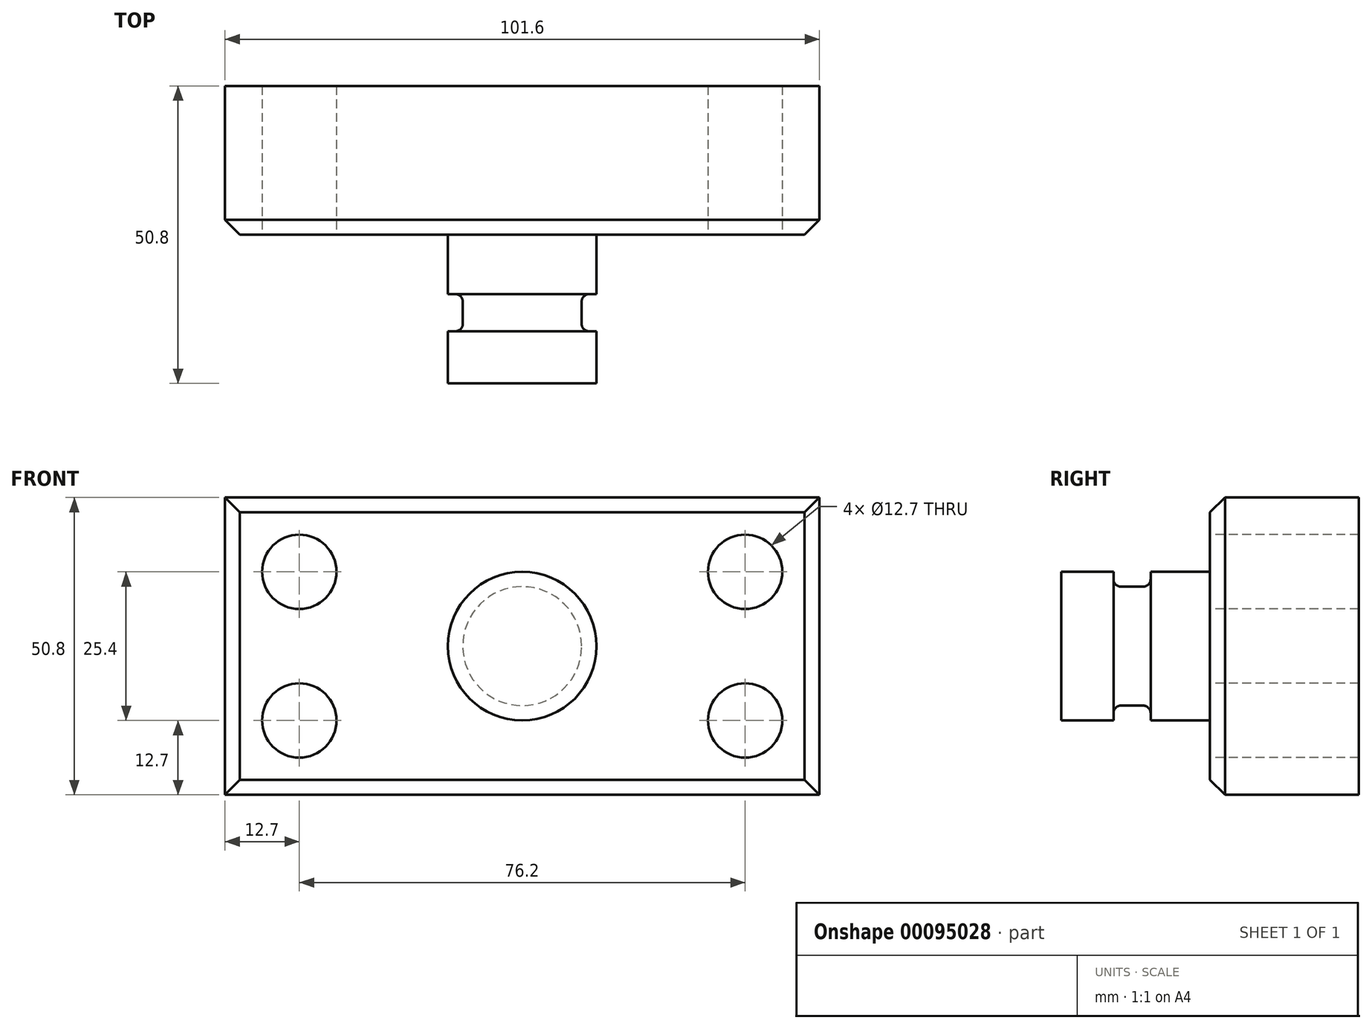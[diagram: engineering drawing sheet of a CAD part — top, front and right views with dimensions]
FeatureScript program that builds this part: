
annotation { "Feature Type Name" : "Feature", "Feature Type Description" : "" }
export const myFeature = defineFeature(function(context is Context, id is Id, definition is map)
    precondition{}
    {
        {
            var Q0;
            Q0=qCreatedBy(makeId("Front.planeOp"),FACE);
            var sketch = newSketch(context, id + "F0", { "sketchPlane" : qUnion([Q0])});
            skLineSegment(sketch, "E0.bottom", {"start": v(50.8, 25.4) * mm, "end": v(-50.8, 25.4) * mm});
            skLineSegment(sketch, "E0.top", {"start": v(50.8, -25.4) * mm, "end": v(-50.8, -25.4) * mm});
            skLineSegment(sketch, "E0.left", {"start": v(50.8, 25.4) * mm, "end": v(50.8, -25.4) * mm});
            skLineSegment(sketch, "E0.right", {"start": v(-50.8, 25.4) * mm, "end": v(-50.8, -25.4) * mm});
            skPoint(sketch, "E0.middle", {"position": v(0, 0) * mm});
            skSolve(sketch);
        }
        {
            var Q0;
            Q0 = qSketchRegion(id + "F0", true);
            extrude(context, id + "F1", {"entities" : qUnion([Q0]), "depth" : 25.4 * mm});
        }
        {
            var Q0;
            Q0=makeQuery(id+"F1.opExtrude","CAP_FACE",FACE,{"disambiguationData":[OSD([sQuery(id+"F0.wireOp",EDGE,"E0.bottom"),sQuery(id+"F0.wireOp",EDGE,"E0.top"),sQuery(id+"F0.wireOp",EDGE,"E0.left"),sQuery(id+"F0.wireOp",EDGE,"E0.right")])],"isStart":false});
            var sketch = newSketch(context, id + "F2", { "sketchPlane" : qUnion([Q0])});
            skCircle(sketch, "E1", {"center": v(-38.1, 12.7) * mm, "radius": 6.35 * mm});
            skCircle(sketch, "E2", {"center": v(-38.1, -12.7) * mm, "radius": 6.35 * mm});
            skCircle(sketch, "E3", {"center": v(38.1, 12.7) * mm, "radius": 6.35 * mm});
            skCircle(sketch, "E4", {"center": v(38.1, -12.7) * mm, "radius": 6.35 * mm});
            skSolve(sketch);
        }
        {
            var Q0;
            Q0=makeQuery(id+"F2.imprint","IMPRINT",FACE,{"disambiguationData":[TD([[makeQuery(id+"F2.imprint","IMPRINT",EDGE,{"derivedFrom":sQuery(id+"F2.wireOp",EDGE,"E1")}),1.0]])]});
            var Q1;
            Q1=makeQuery(id+"F2.imprint","IMPRINT",FACE,{"disambiguationData":[TD([[makeQuery(id+"F2.imprint","IMPRINT",EDGE,{"derivedFrom":sQuery(id+"F2.wireOp",EDGE,"E2")}),1.0]])]});
            var Q2;
            Q2=makeQuery(id+"F2.imprint","IMPRINT",FACE,{"disambiguationData":[TD([[makeQuery(id+"F2.imprint","IMPRINT",EDGE,{"derivedFrom":sQuery(id+"F2.wireOp",EDGE,"E3")}),1.0]])]});
            var Q3;
            Q3=makeQuery(id+"F2.imprint","IMPRINT",FACE,{"disambiguationData":[TD([[makeQuery(id+"F2.imprint","IMPRINT",EDGE,{"derivedFrom":sQuery(id+"F2.wireOp",EDGE,"E4")}),1.0]])]});
            extrude(context, id + "F3", {"entities" : qUnion([Q0, Q1, Q2, Q3]), "operationType" : NewBodyOperationType.REMOVE, "endBound" : BoundingType.THROUGH_ALL, "oppositeDirection" : true, "depth" : 25.4 * mm});
        }
        {
            var Q0;
            Q0=qCreatedBy(makeId("Top.planeOp"),FACE);
            var sketch = newSketch(context, id + "F4", { "sketchPlane" : qUnion([Q0])});
            skLineSegment(sketch, "E5.bottom", {"start": v(12.7, -50.8) * mm, "end": v(0, -50.8) * mm});
            skLineSegment(sketch, "E5.top", {"start": v(12.7, -25.4) * mm, "end": v(0, -25.4) * mm});
            skLineSegment(sketch, "E5.left", {"start": v(12.7, -50.8) * mm, "end": v(12.7, -25.4) * mm});
            skLineSegment(sketch, "E5.right", {"start": v(0, -50.8) * mm, "end": v(0, -25.4) * mm});
            skSolve(sketch);
        }
        {
            var Q0;
            Q0 = qSketchRegion(id + "F4", true);
            var Q1;
            Q1=sQuery(id+"F4.wireOp",EDGE,"E5.right");
            revolve(context, id + "F5", {"operationType" : NewBodyOperationType.ADD, "entities" : qUnion([Q0]), "axis" : qUnion([Q1]), "revolveType" : RevolveType.FULL});
        }
        {
            var Q0;
            Q0=qCreatedBy(makeId("Top.planeOp"),FACE);
            var sketch = newSketch(context, id + "F6", { "sketchPlane" : qUnion([Q0])});
            skLineSegment(sketch, "E6.bottom", {"start": v(-18.46, -41.91) * mm, "end": v(-10.16, -41.91) * mm});
            skLineSegment(sketch, "E6.top", {"start": v(-18.46, -35.56) * mm, "end": v(-10.16, -35.56) * mm});
            skLineSegment(sketch, "E6.left", {"start": v(-18.46, -41.91) * mm, "end": v(-18.46, -35.56) * mm});
            skLineSegment(sketch, "E6.right", {"start": v(-10.16, -41.91) * mm, "end": v(-10.16, -35.56) * mm});
            skLineSegment(sketch, "E7", {"start": v(0, 0) * mm, "end": v(0, -81.51) * mm, "construction": true});
            skSolve(sketch);
        }
        {
            var Q0;
            Q0 = qSketchRegion(id + "F6", true);
            var Q1;
            Q1=sQuery(id+"F6.wireOp",EDGE,"E7");
            revolve(context, id + "F7", {"operationType" : NewBodyOperationType.REMOVE, "entities" : qUnion([Q0]), "axis" : qUnion([Q1]), "revolveType" : RevolveType.FULL, "oppositeDirection" : true});
        }
        {
            var Q0;
            Q0=makeQuery(id+"F5.opRevolve","SWEPT_EDGE",EDGE,{"disambiguationData":[OSD([sQuery(id+"F4.wireOp",EDGE,"E5.top"),sQuery(id+"F4.wireOp",EDGE,"E5.left")])]});
            var Q1;
            Q1=makeQuery(id+"F7.boolean.opBoolean","COPY",EDGE,{"derivedFrom":makeQuery(id+"F7.opRevolve","SWEPT_EDGE",EDGE,{"disambiguationData":[OSD([sQuery(id+"F6.wireOp",EDGE,"E6.top"),sQuery(id+"F6.wireOp",EDGE,"E6.right")])]})});
            var Q2;
            Q2=makeQuery(id+"F7.boolean.opBoolean","COPY",EDGE,{"derivedFrom":makeQuery(id+"F7.opRevolve","SWEPT_EDGE",EDGE,{"disambiguationData":[OSD([sQuery(id+"F6.wireOp",EDGE,"E6.bottom"),sQuery(id+"F6.wireOp",EDGE,"E6.right")])]})});
            fillet(context, id + "F8", {"entities" : qUnion([Q0, Q1, Q2]), "radius" : 1.27 * mm, "tangentPropagation" : true, "allowEdgeOverflow" : false});
        }
        {
            var Q0;
            Q0=makeQuery(id+"F1.opExtrude","CAP_EDGE",EDGE,{"disambiguationData":[OSD([sQuery(id+"F0.wireOp",EDGE,"E0.bottom")])],"isStart":false});
            var Q1;
            Q1=makeQuery(id+"F1.opExtrude","CAP_EDGE",EDGE,{"disambiguationData":[OSD([sQuery(id+"F0.wireOp",EDGE,"E0.right")])],"isStart":false});
            var Q2;
            Q2=makeQuery(id+"F1.opExtrude","CAP_EDGE",EDGE,{"disambiguationData":[OSD([sQuery(id+"F0.wireOp",EDGE,"E0.top")])],"isStart":false});
            var Q3;
            Q3=makeQuery(id+"F1.opExtrude","CAP_EDGE",EDGE,{"disambiguationData":[OSD([sQuery(id+"F0.wireOp",EDGE,"E0.left")])],"isStart":false});
            chamfer(context, id + "F9", {"entities" : qUnion([Q0, Q1, Q2, Q3]), "width" : 2.54 * mm, "tangentPropagation" : true});
        }
    });
